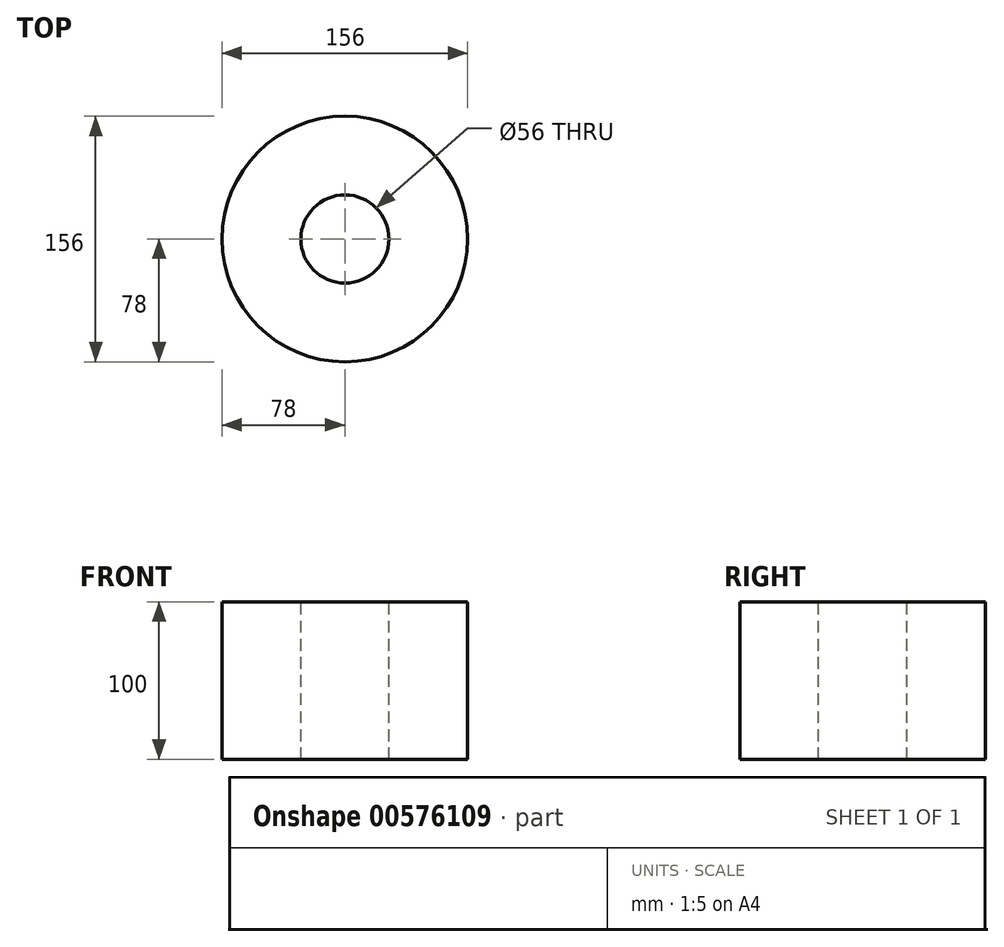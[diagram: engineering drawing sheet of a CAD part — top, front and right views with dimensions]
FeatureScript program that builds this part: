
annotation { "Feature Type Name" : "Feature", "Feature Type Description" : "" }
export const myFeature = defineFeature(function(context is Context, id is Id, definition is map)
    precondition{}
    {
        {
            var Q0;
            Q0=qCreatedBy(makeId("Front.planeOp"),FACE);
            var sketch = newSketch(context, id + "F0", { "sketchPlane" : qUnion([Q0])});
            skLineSegment(sketch, "E0.bottom", {"start": v(28, 50) * mm, "end": v(78, 50) * mm});
            skLineSegment(sketch, "E0.top", {"start": v(28, -50) * mm, "end": v(78, -50) * mm});
            skLineSegment(sketch, "E0.left", {"start": v(28, 50) * mm, "end": v(28, -50) * mm});
            skLineSegment(sketch, "E0.right", {"start": v(78, 50) * mm, "end": v(78, -50) * mm});
            skLineSegment(sketch, "E1", {"start": v(0, 0) * mm, "end": v(0, -79.37) * mm, "construction": true});
            skSolve(sketch);
        }
        {
            var Q0;
            Q0=makeQuery(id+"F0.imprint","IMPRINT",FACE,{"disambiguationData":[TD([[makeQuery(id+"F0.imprint","IMPRINT",EDGE,{"derivedFrom":sQuery(id+"F0.wireOp",EDGE,"E0.bottom")}),-1.0]])]});
            var Q1;
            Q1=sQuery(id+"F0.wireOp",EDGE,"E1");
            revolve(context, id + "F1", {"entities" : qUnion([Q0]), "axis" : qUnion([Q1]), "revolveType" : RevolveType.FULL});
        }
    });
